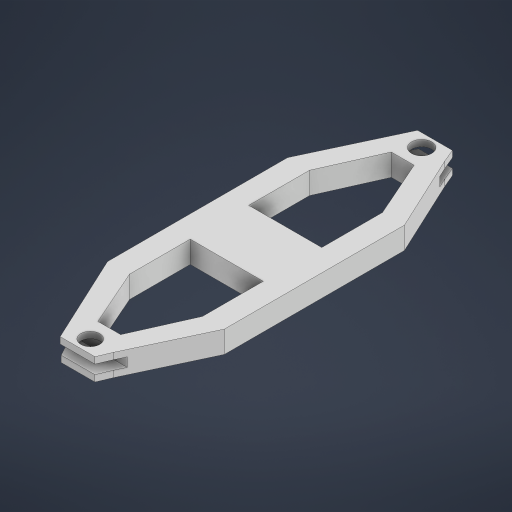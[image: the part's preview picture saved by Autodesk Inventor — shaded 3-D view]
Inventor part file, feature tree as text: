
AUTODESK INVENTOR PART (.ipt)
format: ipt  version: 2023 (Build 270158000, 158)  size: 302,080 bytes
history: native  units: in
note: dims shown in document units (in); Inventor stores cm internally (conversion verified against a paired STEP export)
features: extrude x7, sketch x7
ambient origin geometry x8: Origin, YZ Plane, XZ Plane, XY Plane, X Axis, Y Axis, Z Axis, Center Point
bodies: Solid1 (feature_tree)
feature tree (14):
  extrude  "Extrusion1"  Depth=0.75in TaperAngle=0.0deg
  extrude  "Extrusion9"  Depth=0.75in
  extrude  "Extrusion10"  Depth=4.0in
  extrude  "Extrusion11"  Depth=2.0in
  extrude  "Extrusion12"  TaperAngle=180.0deg  [1 undecoded]
  extrude  "Extrusion13"  Depth=0.75in TaperAngle=0.0deg
  extrude  "Extrusion14"  Depth=0.219in TaperAngle=0.0deg
  sketch  "Sketch1"  dims[d3=0.75in d8=0.75in d9=0.0in]
  sketch  "Sketch9"  dims[d49=11.0236in d50=0.75in]
  sketch  "Sketch10"  dims[d51=0.7902in d52=4.0in]
  sketch  "Sketch11"  dims[d53=2.0in d55=0.3125in]
  sketch  "Sketch12"  dims[d56=0.445in d57=180.0deg]
  sketch  "Sketch13"  dims[d58=0.75in d59=0.0in d60=0.75in d61=0.0in]
  sketch  "Sketch14"  dims[d63=0.219in d64=1.0in d65=0.0in d66=0.0in d67=0.0in d68=0.645in d69=0.69in d70=11.3386in d71=11.3386in d72=1.0in d73=0.0in d74=0.0in d75=0.0in d76=0.445in]
note: 1 required parameter value undecoded (feature->parameter linkage not recoverable at this tier; creation-order binding heuristic only, values carry confidence <= 0.55)
